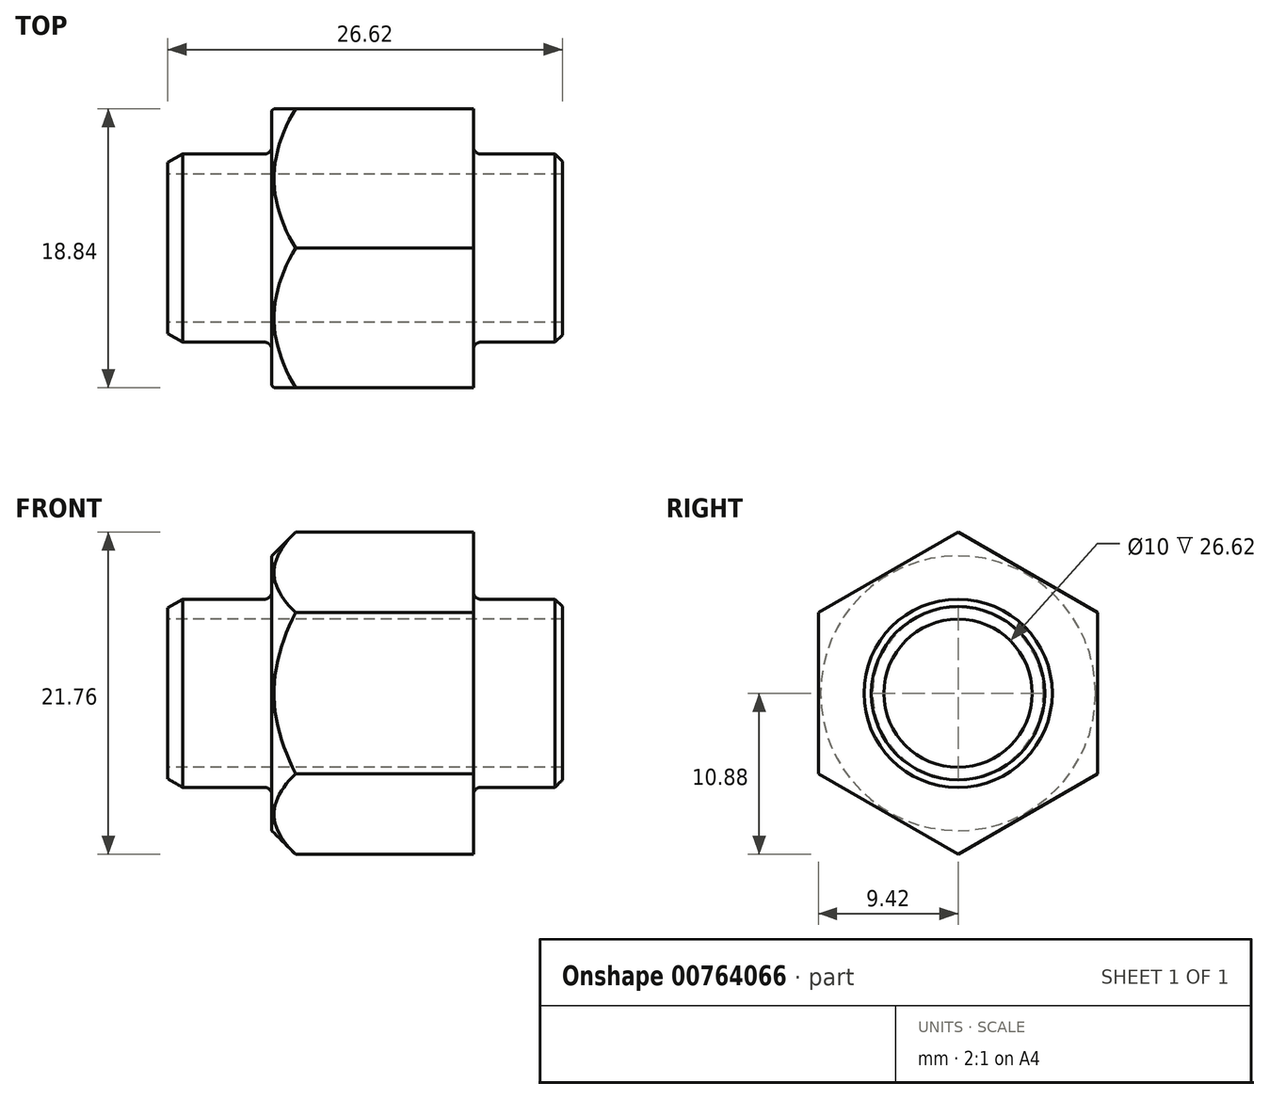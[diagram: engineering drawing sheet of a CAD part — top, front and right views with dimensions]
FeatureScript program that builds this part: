
annotation { "Feature Type Name" : "Feature", "Feature Type Description" : "" }
export const myFeature = defineFeature(function(context is Context, id is Id, definition is map)
    precondition{}
    {
        {
            var Q0;
            Q0=qCreatedBy(makeId("Right.planeOp"),FACE);
            var sketch = newSketch(context, id + "F0", { "sketchPlane" : qUnion([Q0])});
            skCircle(sketch, "E0", {"center": v(0, 0) * mm, "radius": 6.35 * mm});
            skCircle(sketch, "E1.cCircle", {"center": v(0, 0) * mm, "radius": 9.42 * mm, "construction": true});
            skLineSegment(sketch, "E1.0", {"start": v(0, 10.88) * mm, "end": v(9.42, 5.44) * mm});
            skLineSegment(sketch, "E1.1", {"start": v(9.42, 5.44) * mm, "end": v(9.42, -5.44) * mm});
            skLineSegment(sketch, "E1.2", {"start": v(9.42, -5.44) * mm, "end": v(0, -10.88) * mm});
            skLineSegment(sketch, "E1.3", {"start": v(0, -10.88) * mm, "end": v(-9.42, -5.44) * mm});
            skLineSegment(sketch, "E1.4", {"start": v(-9.42, -5.44) * mm, "end": v(-9.42, 5.44) * mm});
            skLineSegment(sketch, "E1.5", {"start": v(-9.42, 5.44) * mm, "end": v(0, 10.88) * mm});
            skPoint(sketch, "E1.0.midPoint", {"position": v(4.7, 8.16) * mm});
            skSolve(sketch);
        }
        {
            var Q0;
            Q0=makeQuery(id+"F0.imprint","IMPRINT",FACE,{"disambiguationData":[TD([[makeQuery(id+"F0.imprint","IMPRINT",EDGE,{"derivedFrom":sQuery(id+"F0.wireOp",EDGE,"E0")}),-1.0]])]});
            var Q1;
            Q1=makeQuery(id+"F0.imprint","IMPRINT",FACE,{"disambiguationData":[TD([[makeQuery(id+"F0.imprint","IMPRINT",EDGE,{"derivedFrom":sQuery(id+"F0.wireOp",EDGE,"E0")}),1.0]])]});
            extrude(context, id + "F1", {"entities" : qUnion([Q0, Q1]), "depth" : 6.8 * mm, "hasSecondDirection" : true, "secondDirectionOppositeDirection" : true, "secondDirectionDepth" : 6.8 * mm});
        }
        {
            var Q0;
            Q0=makeQuery(id+"F0.imprint","IMPRINT",FACE,{"disambiguationData":[TD([[makeQuery(id+"F0.imprint","IMPRINT",EDGE,{"derivedFrom":sQuery(id+"F0.wireOp",EDGE,"E0")}),1.0]])]});
            extrude(context, id + "F2", {"entities" : qUnion([Q0]), "operationType" : NewBodyOperationType.ADD, "oppositeDirection" : true, "depth" : 13.82 * mm, "hasSecondDirection" : true, "secondDirectionOppositeDirection" : false, "secondDirectionDepth" : 12.8 * mm});
        }
        {
            var Q0;
            Q0=qCreatedBy(makeId("Front.planeOp"),FACE);
            var sketch = newSketch(context, id + "F3", { "sketchPlane" : qUnion([Q0])});
            skLineSegment(sketch, "E2.0", {"start": v(-5.2, 10.88) * mm, "end": v(-6.8, 10.88) * mm});
            skLineSegment(sketch, "E2.1", {"start": v(-6.8, 9.28) * mm, "end": v(-6.8, 10.88) * mm});
            skLineSegment(sketch, "E3", {"start": v(-6.8, 9.28) * mm, "end": v(-5.2, 10.88) * mm});
            skPoint(sketch, "E4.orphan", {"position": v(6.8, 10.88) * mm});
            skPoint(sketch, "E5.orphan", {"position": v(-6.8, 5.44) * mm});
            skSolve(sketch);
        }
        {
            var Q0;
            Q0=makeQuery(id+"F3.imprint","IMPRINT",FACE,{"disambiguationData":[TD([[makeQuery(id+"F3.imprint","IMPRINT",EDGE,{"derivedFrom":sQuery(id+"F3.wireOp",EDGE,"E2.0")}),1.0]])]});
            var Q1;
            {var subQ0=sQuery(id+"F0.wireOp",EDGE,"E0");Q1=makeQuery(id+"F2.boolean.opBoolean","SPLIT",FACE,{"disambiguationData":[TD([makeQuery(id+"F2.opExtrude","CAP_FACE",FACE,{"disambiguationData":[OSD([subQ0])],"isStart":true})])],"derivedFrom":makeQuery(id+"F2.opExtrude","SWEPT_FACE",FACE,{"disambiguationData":[OSD([subQ0])]})});}
            revolve(context, id + "F4", {"operationType" : NewBodyOperationType.REMOVE, "entities" : qUnion([Q0]), "axis" : qUnion([Q1]), "revolveType" : RevolveType.FULL, "oppositeDirection" : true});
        }
        {
            var Q0;
            Q0=qCreatedBy(makeId("Right.planeOp"),FACE);
            var sketch = newSketch(context, id + "F5", { "sketchPlane" : qUnion([Q0])});
            skCircle(sketch, "E6", {"center": v(0, 0) * mm, "radius": 5 * mm});
            skSolve(sketch);
        }
        {
            var Q0;
            Q0=makeQuery(id+"F5.imprint","IMPRINT",FACE,{"disambiguationData":[TD([[makeQuery(id+"F5.imprint","IMPRINT",EDGE,{"derivedFrom":sQuery(id+"F5.wireOp",EDGE,"E6")}),1.0]])]});
            extrude(context, id + "F6", {"entities" : qUnion([Q0]), "operationType" : NewBodyOperationType.REMOVE, "endBound" : BoundingType.SYMMETRIC, "depth" : 30 * mm});
        }
        {
            var Q0;
            Q0=makeQuery(id+"F2.opExtrude","CAP_EDGE",EDGE,{"disambiguationData":[OSD([sQuery(id+"F0.wireOp",EDGE,"E0")])],"isStart":false});
            chamfer(context, id + "F7", {"entities" : qUnion([Q0]), "chamferType" : ChamferType.OFFSET_ANGLE, "width" : 1 * mm, "oppositeDirection" : false, "angle" : 30 * degree, "tangentPropagation" : true});
        }
        {
            var Q0;
            Q0=makeQuery(id+"F2.opExtrude","CAP_EDGE",EDGE,{"disambiguationData":[OSD([sQuery(id+"F0.wireOp",EDGE,"E0")])],"isStart":true});
            chamfer(context, id + "F8", {"entities" : qUnion([Q0]), "width" : 0.5 * mm, "tangentPropagation" : true});
        }
        {
            var Q0;
            Q0=makeQuery(id+"F2.boolean.opBoolean","INTERSECT",EDGE,{"derivedFrom":[makeQuery(id+"F1.opExtrude","CAP_FACE",FACE,{"disambiguationData":[OSD([sQuery(id+"F0.wireOp",EDGE,"E1.0"),sQuery(id+"F0.wireOp",EDGE,"E1.1"),sQuery(id+"F0.wireOp",EDGE,"E1.2"),sQuery(id+"F0.wireOp",EDGE,"E1.3"),sQuery(id+"F0.wireOp",EDGE,"E1.4"),sQuery(id+"F0.wireOp",EDGE,"E1.5")])],"isStart":false}),makeQuery(id+"F2.opExtrude","SWEPT_FACE",FACE,{"disambiguationData":[OSD([sQuery(id+"F0.wireOp",EDGE,"E0")])]})]});
            var Q1;
            Q1=makeQuery(id+"F2.boolean.opBoolean","INTERSECT",EDGE,{"derivedFrom":[makeQuery(id+"F1.opExtrude","CAP_FACE",FACE,{"disambiguationData":[OSD([sQuery(id+"F0.wireOp",EDGE,"E1.0"),sQuery(id+"F0.wireOp",EDGE,"E1.1"),sQuery(id+"F0.wireOp",EDGE,"E1.2"),sQuery(id+"F0.wireOp",EDGE,"E1.3"),sQuery(id+"F0.wireOp",EDGE,"E1.4"),sQuery(id+"F0.wireOp",EDGE,"E1.5")])],"isStart":true}),makeQuery(id+"F2.opExtrude","SWEPT_FACE",FACE,{"disambiguationData":[OSD([sQuery(id+"F0.wireOp",EDGE,"E0")])]})]});
            fillet(context, id + "F9", {"entities" : qUnion([Q0, Q1]), "radius" : 0.5 * mm, "tangentPropagation" : true, "allowEdgeOverflow" : false});
        }
    });
